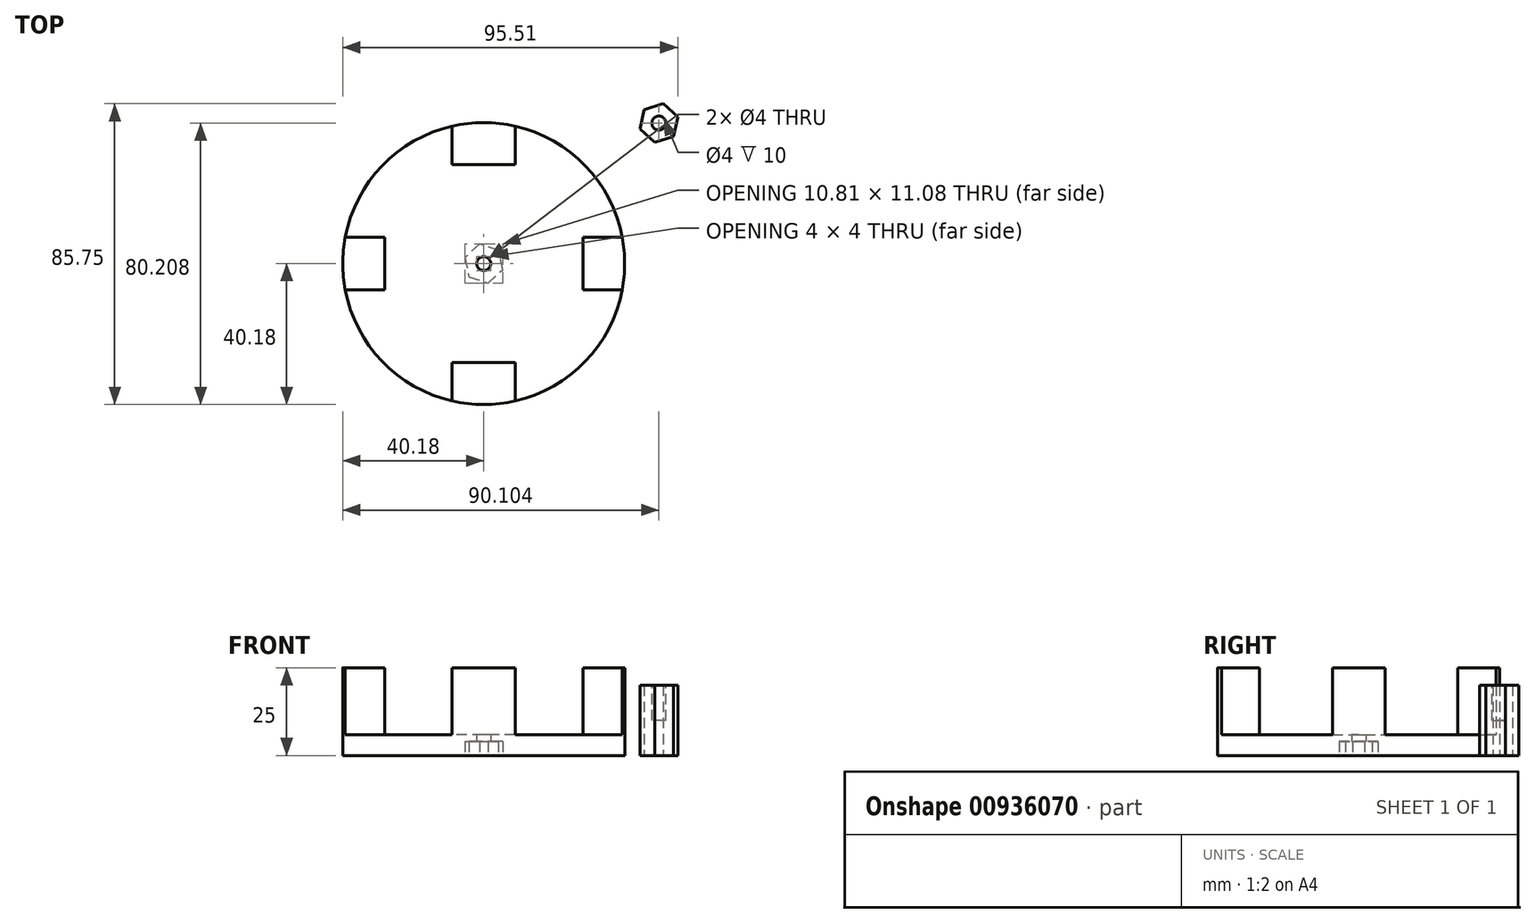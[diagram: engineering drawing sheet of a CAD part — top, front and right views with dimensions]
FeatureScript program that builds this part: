
annotation { "Feature Type Name" : "Feature", "Feature Type Description" : "" }
export const myFeature = defineFeature(function(context is Context, id is Id, definition is map)
    precondition{}
    {
        {
            var Q0;
            Q0=qCreatedBy(makeId("Top.planeOp"),FACE);
            var sketch = newSketch(context, id + "F0", { "sketchPlane" : qUnion([Q0])});
            skLineSegment(sketch, "E0.bottom", {"start": v(9, 28.25) * mm, "end": v(-9, 28.25) * mm});
            skLineSegment(sketch, "E0.top", {"start": v(9, 40.25) * mm, "end": v(-9, 40.25) * mm});
            skLineSegment(sketch, "E0.left", {"start": v(9, 28.25) * mm, "end": v(9, 40.25) * mm});
            skLineSegment(sketch, "E0.right", {"start": v(-9, 28.25) * mm, "end": v(-9, 40.25) * mm});
            skPoint(sketch, "E0.middle", {"position": v(0, 34.25) * mm});
            skLineSegment(sketch, "E1.bottom", {"start": v(9, -40.25) * mm, "end": v(-9, -40.25) * mm});
            skLineSegment(sketch, "E1.top", {"start": v(9, -28.25) * mm, "end": v(-9, -28.25) * mm});
            skLineSegment(sketch, "E1.left", {"start": v(9, -40.25) * mm, "end": v(9, -28.25) * mm});
            skLineSegment(sketch, "E1.right", {"start": v(-9, -40.25) * mm, "end": v(-9, -28.25) * mm});
            skPoint(sketch, "E1.middle", {"position": v(0, -34.25) * mm});
            skLineSegment(sketch, "E2.bottom", {"start": v(40.25, -7.5) * mm, "end": v(28.25, -7.5) * mm});
            skLineSegment(sketch, "E2.top", {"start": v(40.25, 7.5) * mm, "end": v(28.25, 7.5) * mm});
            skLineSegment(sketch, "E2.left", {"start": v(40.25, -7.5) * mm, "end": v(40.25, 7.5) * mm});
            skLineSegment(sketch, "E2.right", {"start": v(28.25, -7.5) * mm, "end": v(28.25, 7.5) * mm});
            skPoint(sketch, "E2.middle", {"position": v(34.25, 0) * mm});
            skLineSegment(sketch, "E3.bottom", {"start": v(-40.25, 7.5) * mm, "end": v(-28.25, 7.5) * mm});
            skLineSegment(sketch, "E3.top", {"start": v(-40.25, -7.5) * mm, "end": v(-28.25, -7.5) * mm});
            skLineSegment(sketch, "E3.left", {"start": v(-40.25, 7.5) * mm, "end": v(-40.25, -7.5) * mm});
            skLineSegment(sketch, "E3.right", {"start": v(-28.25, 7.5) * mm, "end": v(-28.25, -7.5) * mm});
            skPoint(sketch, "E3.middle", {"position": v(-34.25, 0) * mm});
            skCircle(sketch, "E4", {"center": v(0, 0) * mm, "radius": 40.18 * mm});
            skSolve(sketch);
        }
        {
            var Q0;
            {var subQ0=sQuery(id+"F0.wireOp",EDGE,"E3.right");Q0=makeQuery(id+"F0.imprint","IMPRINT",FACE,{"disambiguationData":[TD([[makeQuery(id+"F0.imprint","IMPRINT",EDGE,{"derivedFrom":subQ0}),-1.0]])]});}
            var Q1;
            {var subQ0=sQuery(id+"F0.wireOp",EDGE,"E0.bottom");Q1=makeQuery(id+"F0.imprint","IMPRINT",FACE,{"disambiguationData":[TD([[makeQuery(id+"F0.imprint","IMPRINT",EDGE,{"derivedFrom":subQ0}),-1.0]])]});}
            var Q2;
            {var subQ0=sQuery(id+"F0.wireOp",EDGE,"E2.right");Q2=makeQuery(id+"F0.imprint","IMPRINT",FACE,{"disambiguationData":[TD([[makeQuery(id+"F0.imprint","IMPRINT",EDGE,{"derivedFrom":subQ0}),-1.0]])]});}
            var Q3;
            {var subQ0=sQuery(id+"F0.wireOp",EDGE,"E1.top");Q3=makeQuery(id+"F0.imprint","IMPRINT",FACE,{"disambiguationData":[TD([[makeQuery(id+"F0.imprint","IMPRINT",EDGE,{"derivedFrom":subQ0}),1.0]])]});}
            extrude(context, id + "F1", {"entities" : qUnion([Q0, Q1, Q2, Q3]), "depth" : 25 * mm, "offsetDistance" : 25 * mm});
        }
        {
            var Q0;
            {var subQ10=sQuery(id+"F0.wireOp",EDGE,"E0.bottom");Q0=makeQuery(id+"F0.imprint","IMPRINT",FACE,{"disambiguationData":[TD([[makeQuery(id+"F0.imprint","IMPRINT",EDGE,{"derivedFrom":subQ10}),1.0]])]});}
            extrude(context, id + "F2", {"entities" : qUnion([Q0]), "operationType" : NewBodyOperationType.ADD, "depth" : 6 * mm, "offsetDistance" : 25 * mm});
        }
        {
            var Q0;
            {var subQ0=sQuery(id+"F0.wireOp",EDGE,"E4");var subQ1=sQuery(id+"F0.wireOp",EDGE,"E3.right");var subQ2=sQuery(id+"F0.wireOp",EDGE,"E3.top");var subQ3=sQuery(id+"F0.wireOp",EDGE,"E3.bottom");var subQ4=sQuery(id+"F0.wireOp",EDGE,"E2.right");var subQ5=sQuery(id+"F0.wireOp",EDGE,"E2.top");var subQ6=sQuery(id+"F0.wireOp",EDGE,"E2.bottom");var subQ7=sQuery(id+"F0.wireOp",EDGE,"E1.right");var subQ8=sQuery(id+"F0.wireOp",EDGE,"E1.left");var subQ9=sQuery(id+"F0.wireOp",EDGE,"E1.top");var subQ10=sQuery(id+"F0.wireOp",EDGE,"E0.right");var subQ11=sQuery(id+"F0.wireOp",EDGE,"E0.left");var subQ12=sQuery(id+"F0.wireOp",EDGE,"E0.bottom");Q0=makeQuery(id+"F2.boolean.opBoolean","MERGE",FACE,{"derivedFrom":[makeQuery(id+"F1.opExtrude","CAP_FACE",FACE,{"disambiguationData":[OSD([subQ12,subQ11,subQ10,subQ0])],"isStart":true}),makeQuery(id+"F1.opExtrude","CAP_FACE",FACE,{"disambiguationData":[OSD([subQ9,subQ8,subQ7,subQ0])],"isStart":true}),makeQuery(id+"F1.opExtrude","CAP_FACE",FACE,{"disambiguationData":[OSD([subQ6,subQ5,subQ4,subQ0])],"isStart":true}),makeQuery(id+"F1.opExtrude","CAP_FACE",FACE,{"disambiguationData":[OSD([subQ3,subQ2,subQ1,subQ0])],"isStart":true}),makeQuery(id+"F2.opExtrude","CAP_FACE",FACE,{"disambiguationData":[OSD([subQ12,subQ11,subQ10,subQ9,subQ8,subQ7,subQ6,subQ5,subQ4,subQ3,subQ2,subQ1,subQ0])],"isStart":true})]});}
            var sketch = newSketch(context, id + "F3", { "sketchPlane" : qUnion([Q0])});
            skCircle(sketch, "E5.cCircle", {"center": v(0, 0) * mm, "radius": 5.67 * mm, "construction": true});
            skLineSegment(sketch, "E5.0", {"start": v(4.19, -3.82) * mm, "end": v(-1.22, -5.54) * mm});
            skLineSegment(sketch, "E5.1", {"start": v(-1.22, -5.54) * mm, "end": v(-5.4, -1.72) * mm});
            skLineSegment(sketch, "E5.2", {"start": v(-5.4, -1.72) * mm, "end": v(-4.19, 3.82) * mm});
            skLineSegment(sketch, "E5.3", {"start": v(-4.19, 3.82) * mm, "end": v(1.22, 5.54) * mm});
            skLineSegment(sketch, "E5.4", {"start": v(1.22, 5.54) * mm, "end": v(5.4, 1.72) * mm});
            skLineSegment(sketch, "E5.5", {"start": v(5.4, 1.72) * mm, "end": v(4.19, -3.82) * mm});
            skSolve(sketch);
        }
        {
            var Q0;
            Q0=makeQuery(id+"F3.imprint","IMPRINT",FACE,{"disambiguationData":[TD([[makeQuery(id+"F3.imprint","IMPRINT",EDGE,{"derivedFrom":sQuery(id+"F3.wireOp",EDGE,"E5.0")}),-1.0]])]});
            extrude(context, id + "F4", {"entities" : qUnion([Q0]), "operationType" : NewBodyOperationType.REMOVE, "oppositeDirection" : true, "depth" : 4 * mm, "offsetDistance" : 25 * mm});
        }
        {
            var Q0;
            Q0=makeQuery(id+"F4.boolean.opBoolean","COPY",FACE,{"derivedFrom":makeQuery(id+"F4.opExtrude","CAP_FACE",FACE,{"disambiguationData":[OSD([sQuery(id+"F3.wireOp",EDGE,"E5.0"),sQuery(id+"F3.wireOp",EDGE,"E5.1"),sQuery(id+"F3.wireOp",EDGE,"E5.2"),sQuery(id+"F3.wireOp",EDGE,"E5.3"),sQuery(id+"F3.wireOp",EDGE,"E5.4"),sQuery(id+"F3.wireOp",EDGE,"E5.5")])],"isStart":false})});
            var sketch = newSketch(context, id + "F5", { "sketchPlane" : qUnion([Q0])});
            skCircle(sketch, "E6", {"center": v(0, 0) * mm, "radius": 2 * mm});
            skSolve(sketch);
        }
        {
            var Q0;
            Q0=makeQuery(id+"F5.imprint","IMPRINT",FACE,{"disambiguationData":[TD([[makeQuery(id+"F5.imprint","IMPRINT",EDGE,{"derivedFrom":sQuery(id+"F5.wireOp",EDGE,"E6")}),1.0]])]});
            extrude(context, id + "F6", {"entities" : qUnion([Q0]), "operationType" : NewBodyOperationType.REMOVE, "oppositeDirection" : true, "depth" : 25 * mm, "offsetDistance" : 25 * mm});
        }
        {
            var Q0;
            Q0=qCreatedBy(makeId("Top.planeOp"),FACE);
            var sketch = newSketch(context, id + "F7", { "sketchPlane" : qUnion([Q0])});
            skCircle(sketch, "E7.cCircle", {"center": v(49.92, 40.03) * mm, "radius": 5.67 * mm, "construction": true});
            skLineSegment(sketch, "E7.0", {"start": v(54.11, 36.2) * mm, "end": v(48.7, 34.49) * mm});
            skLineSegment(sketch, "E7.1", {"start": v(48.7, 34.49) * mm, "end": v(44.52, 38.31) * mm});
            skLineSegment(sketch, "E7.2", {"start": v(44.52, 38.31) * mm, "end": v(45.73, 43.85) * mm});
            skLineSegment(sketch, "E7.3", {"start": v(45.73, 43.85) * mm, "end": v(51.14, 45.57) * mm});
            skLineSegment(sketch, "E7.4", {"start": v(51.14, 45.57) * mm, "end": v(55.33, 41.74) * mm});
            skLineSegment(sketch, "E7.5", {"start": v(55.33, 41.74) * mm, "end": v(54.11, 36.2) * mm});
            skSolve(sketch);
        }
        {
            var Q0;
            Q0=makeQuery(id+"F7.imprint","IMPRINT",FACE,{"disambiguationData":[TD([[makeQuery(id+"F7.imprint","IMPRINT",EDGE,{"derivedFrom":sQuery(id+"F7.wireOp",EDGE,"E7.0")}),-1.0]])]});
            extrude(context, id + "F8", {"entities" : qUnion([Q0]), "depth" : 20 * mm, "offsetDistance" : 25 * mm});
        }
        {
            var Q0;
            Q0=makeQuery(id+"F8.opExtrude","CAP_FACE",FACE,{"disambiguationData":[OSD([sQuery(id+"F7.wireOp",EDGE,"E7.0"),sQuery(id+"F7.wireOp",EDGE,"E7.1"),sQuery(id+"F7.wireOp",EDGE,"E7.2"),sQuery(id+"F7.wireOp",EDGE,"E7.3"),sQuery(id+"F7.wireOp",EDGE,"E7.4"),sQuery(id+"F7.wireOp",EDGE,"E7.5")])],"isStart":false});
            var sketch = newSketch(context, id + "F9", { "sketchPlane" : qUnion([Q0])});
            skCircle(sketch, "E8", {"center": v(49.92, 40.03) * mm, "radius": 2 * mm});
            skLineSegment(sketch, "E9", {"start": v(51.14, 45.57) * mm, "end": v(48.7, 34.49) * mm, "construction": true});
            skLineSegment(sketch, "E10", {"start": v(45.13, 41.08) * mm, "end": v(54.72, 38.97) * mm, "construction": true});
            skSolve(sketch);
        }
        {
            var Q0;
            Q0=makeQuery(id+"F9.imprint","IMPRINT",FACE,{"disambiguationData":[TD([[makeQuery(id+"F9.imprint","IMPRINT",EDGE,{"derivedFrom":sQuery(id+"F9.wireOp",EDGE,"E8")}),1.0]])]});
            extrude(context, id + "F10", {"entities" : qUnion([Q0]), "operationType" : NewBodyOperationType.REMOVE, "oppositeDirection" : true, "depth" : 10 * mm, "offsetDistance" : 25 * mm});
        }
        {
            var Q0;
            Q0=makeQuery(id+"F1.opExtrude","SWEPT_BODY",BODY,{"disambiguationData":[OSD([sQuery(id+"F0.wireOp",EDGE,"E0.bottom"),sQuery(id+"F0.wireOp",EDGE,"E0.left"),sQuery(id+"F0.wireOp",EDGE,"E0.right"),sQuery(id+"F0.wireOp",EDGE,"E4")])]});
            transform(context, id + "F11", {"entities" : qUnion([Q0]), "transformType" : TransformType.TRANSLATION_3D, "dx" : 0 * mm, "dy" : 0 * mm, "dz" : 0 * mm, "makeCopy" : true});
        }
    });
